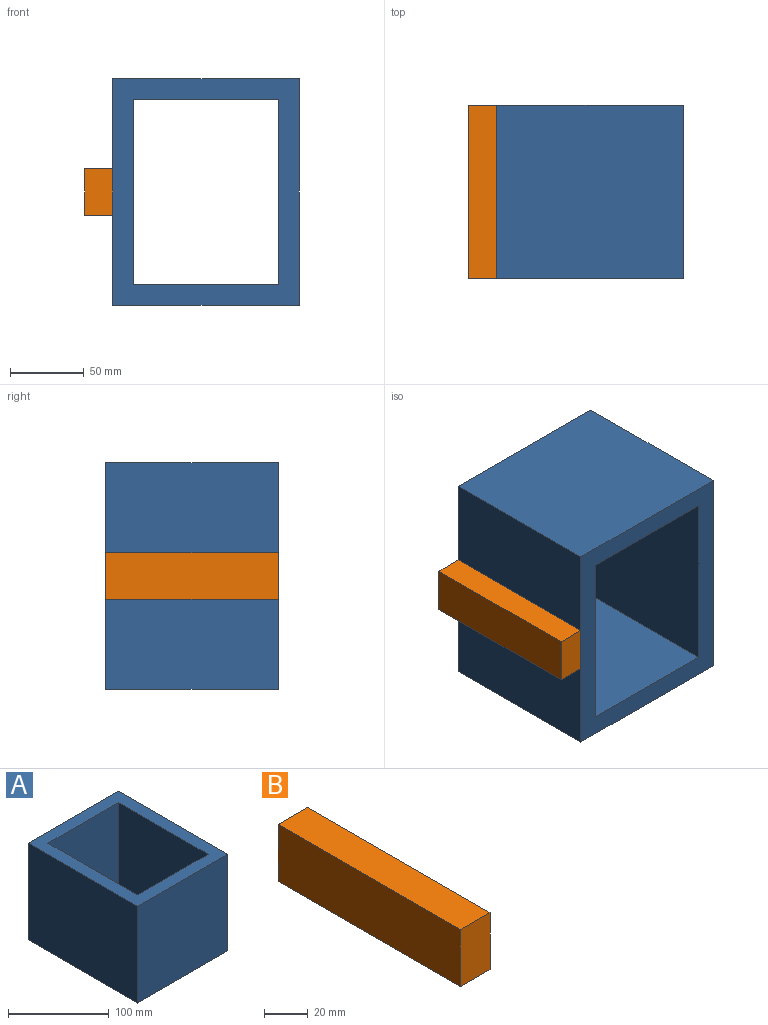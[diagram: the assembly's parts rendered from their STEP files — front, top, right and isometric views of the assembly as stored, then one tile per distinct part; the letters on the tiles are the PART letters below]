
ASSEMBLY  parts=2 mates=1
PART A: 10 faces, bbox 127x154x117.5 mm
  f0: plane 127x117.48mm, normal (0,1,0), area 14919.3mm2, adj f1,f7,f8,f9
  f1: plane 153.99x117.48mm, normal (-1,0,0), area 18089.7mm2, adj f0,f2,f8,f9
  f2: plane 127x117.48mm, normal (0,-1,0), area 14919.3mm2, adj f1,f7,f8,f9
  f3: plane 125.99x117.48mm, normal (1,0,0), area 14800.4mm2, adj f4,f6,f8,f9
  f4: plane 117.48x99mm, normal (0,-1,0), area 11630mm2, adj f3,f5,f8,f9
  f5: plane 125.99x117.48mm, normal (-1,0,0), area 14800.4mm2, adj f4,f6,f8,f9
  f6: plane 117.48x99mm, normal (0,1,0), area 11630mm2, adj f3,f5,f8,f9
  f7: plane 153.99x117.48mm, normal (1,0,0), area 18089.7mm2, adj f0,f2,f8,f9
  f8: plane 153.99x127mm, normal (0,0,1), area 7083.7mm2, adj f0,f1,f2,f3,f4,f5,f6,f7
  f9: plane 153.99x127mm, normal (0,0,-1), area 7083.7mm2, adj f0,f1,f2,f3,f4,f5,f6,f7
PART B: 6 faces, bbox 19.1x117.5x31.8 mm
  f0: plane 117.48x19.05mm, normal (0,0,1), area 2237.9mm2, adj f1,f3,f4,f5
  f1: plane 117.48x31.75mm, normal (-1,0,0), area 3729.8mm2, adj f0,f2,f4,f5
  f2: plane 117.48x19.05mm, normal (0,0,-1), area 2237.9mm2, adj f1,f3,f4,f5
  f3: plane 117.48x31.75mm, normal (1,0,0), area 3729.8mm2, adj f0,f2,f4,f5
  f4: plane 31.75x19.05mm, normal (0,-1,0), area 604.8mm2, adj f0,f1,f2,f3
  f5: plane 31.75x19.05mm, normal (0,1,0), area 604.8mm2, adj f0,f1,f2,f3
PLACE A rot(axis=(0,0.71,0.71),180deg) t=(54.29,-0.58,5.95)mm
PLACE B t=(16.06,116.9,65.25)mm
MATE fastened A.f7 <-> B.f3  axis (-1,0,0) through (33.15,58.16,66.78)mm
